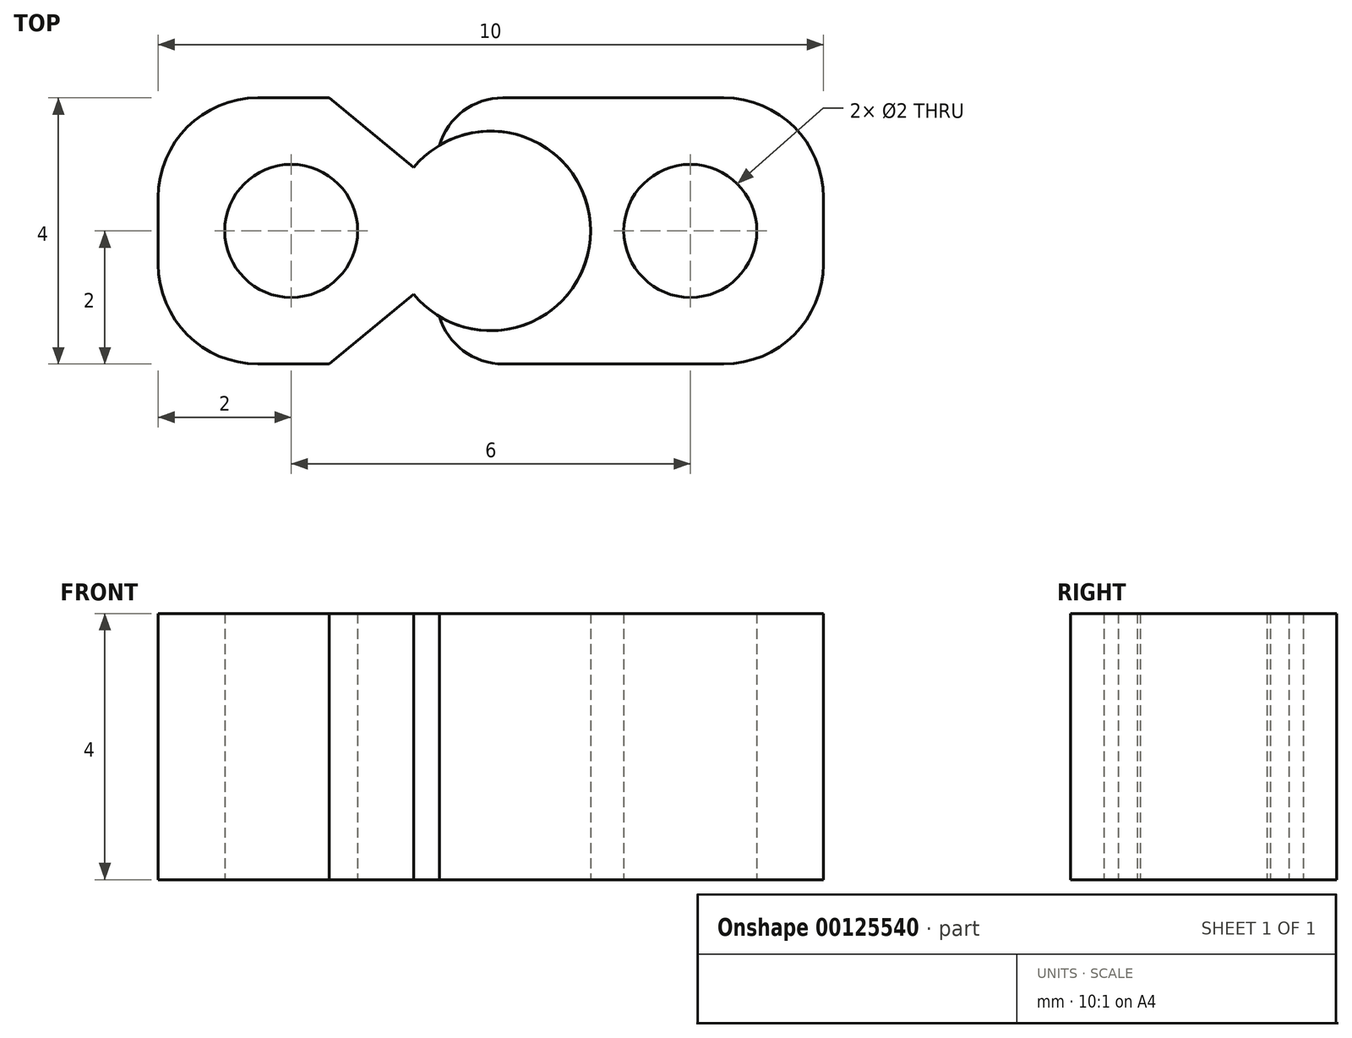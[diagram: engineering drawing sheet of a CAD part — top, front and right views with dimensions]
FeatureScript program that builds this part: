
annotation { "Feature Type Name" : "Feature", "Feature Type Description" : "" }
export const myFeature = defineFeature(function(context is Context, id is Id, definition is map)
    precondition{}
    {
        {
            var Q0;
            Q0=qCreatedBy(makeId("Top.planeOp"),FACE);
            var sketch = newSketch(context, id + "F0", { "sketchPlane" : qUnion([Q0])});
            skLineSegment(sketch, "E0.bottom", {"start": v(5, 2) * mm, "end": v(-5, 2) * mm});
            skLineSegment(sketch, "E0.top", {"start": v(5, -2) * mm, "end": v(-5, -2) * mm});
            skLineSegment(sketch, "E0.left", {"start": v(5, 2) * mm, "end": v(5, -2) * mm});
            skLineSegment(sketch, "E0.right", {"start": v(-5, 2) * mm, "end": v(-5, -2) * mm});
            skPoint(sketch, "E0.middle", {"position": v(0, 0) * mm});
            skCircle(sketch, "E1", {"center": v(0, 0) * mm, "radius": 1.5 * mm});
            skLineSegment(sketch, "E2", {"start": v(-1.16, 0.95) * mm, "end": v(-2.43, 2) * mm});
            skLineSegment(sketch, "E3.0", {"start": v(-0.77, 1.28) * mm, "end": v(-1.64, 2) * mm});
            skLineSegment(sketch, "E4.MirrorCS", {"start": v(-1.16, -0.95) * mm, "end": v(-2.43, -2) * mm});
            skLineSegment(sketch, "E5.MirrorCS", {"start": v(-0.77, -1.28) * mm, "end": v(-1.64, -2) * mm});
            skPoint(sketch, "E6", {"position": v(3, 0) * mm});
            skPoint(sketch, "E7.MirrorP", {"position": v(-3, 0) * mm});
            skSolve(sketch);
        }
        {
            var Q0;
            {var subQ3=sQuery(id+"F0.wireOp",EDGE,"E0.right");Q0=makeQuery(id+"F0.imprint","IMPRINT",FACE,{"disambiguationData":[TD([[makeQuery(id+"F0.imprint","IMPRINT",EDGE,{"derivedFrom":subQ3}),1.0]])]});}
            var Q1;
            {var subQ0=sQuery(id+"F0.wireOp",EDGE,"E1");var subQ1=makeQuery(id+"F0.imprint","INTERSECT",VERTEX,{"derivedFrom":[subQ0,sQuery(id+"F0.wireOp",EDGE,"E2")]});Q1=makeQuery(id+"F0.imprint","IMPRINT",FACE,{"disambiguationData":[TD([[makeQuery(id+"F0.imprint","IMPRINT",EDGE,{"disambiguationData":[TD([[subQ1,1.0]])],"derivedFrom":subQ0}),1.0]])]});}
            extrude(context, id + "F1", {"entities" : qUnion([Q0, Q1]), "depth" : 4 * mm});
        }
        {
            var Q0;
            {var subQ3=sQuery(id+"F0.wireOp",EDGE,"E0.left");Q0=makeQuery(id+"F0.imprint","IMPRINT",FACE,{"disambiguationData":[TD([[makeQuery(id+"F0.imprint","IMPRINT",EDGE,{"derivedFrom":subQ3}),-1.0]])]});}
            extrude(context, id + "F2", {"entities" : qUnion([Q0]), "depth" : 4 * mm});
        }
        {
            var Q0;
            Q0=makeQuery(id+"F1.opExtrude","SWEPT_EDGE",EDGE,{"disambiguationData":[OSD([sQuery(id+"F0.wireOp",EDGE,"E0.top"),sQuery(id+"F0.wireOp",EDGE,"E0.right")])]});
            var Q1;
            Q1=makeQuery(id+"F1.opExtrude","SWEPT_EDGE",EDGE,{"disambiguationData":[OSD([sQuery(id+"F0.wireOp",EDGE,"E0.bottom"),sQuery(id+"F0.wireOp",EDGE,"E0.right")])]});
            var Q2;
            Q2=makeQuery(id+"F2.opExtrude","SWEPT_EDGE",EDGE,{"disambiguationData":[OSD([sQuery(id+"F0.wireOp",EDGE,"E0.top"),sQuery(id+"F0.wireOp",EDGE,"E0.left")])]});
            var Q3;
            Q3=makeQuery(id+"F2.opExtrude","SWEPT_EDGE",EDGE,{"disambiguationData":[OSD([sQuery(id+"F0.wireOp",EDGE,"E0.bottom"),sQuery(id+"F0.wireOp",EDGE,"E0.left")])]});
            fillet(context, id + "F3", {"entities" : qUnion([Q0, Q1, Q2, Q3]), "radius" : 1.5 * mm, "tangentPropagation" : true, "allowEdgeOverflow" : false});
        }
        {
            var Q0;
            Q0=makeQuery(id+"F2.opExtrude","SWEPT_EDGE",EDGE,{"disambiguationData":[OSD([sQuery(id+"F0.wireOp",EDGE,"E0.bottom"),sQuery(id+"F0.wireOp",EDGE,"E3.0")])]});
            var Q1;
            Q1=makeQuery(id+"F2.opExtrude","SWEPT_EDGE",EDGE,{"disambiguationData":[OSD([sQuery(id+"F0.wireOp",EDGE,"E0.top"),sQuery(id+"F0.wireOp",EDGE,"E5.MirrorCS")])]});
            fillet(context, id + "F4", {"entities" : qUnion([Q0, Q1]), "radius" : 1 * mm, "tangentPropagation" : true, "allowEdgeOverflow" : false});
        }
        {
            var Q0;
            Q0=sQuery(id+"F0.wireOp",VERTEX,"E6");
            var Q1;
            Q1=sQuery(id+"F0.wireOp",VERTEX,"E7.MirrorP");
            var Q2;
            Q2=makeQuery(id+"F2.opExtrude","SWEPT_BODY",BODY,{"disambiguationData":[OSD([sQuery(id+"F0.wireOp",EDGE,"E0.bottom"),sQuery(id+"F0.wireOp",EDGE,"E0.top"),sQuery(id+"F0.wireOp",EDGE,"E0.left"),sQuery(id+"F0.wireOp",EDGE,"E1"),sQuery(id+"F0.wireOp",EDGE,"E3.0"),sQuery(id+"F0.wireOp",EDGE,"E5.MirrorCS")])]});
            var Q3;
            Q3=makeQuery(id+"F1.opExtrude","SWEPT_BODY",BODY,{"disambiguationData":[OSD([sQuery(id+"F0.wireOp",EDGE,"E0.bottom"),sQuery(id+"F0.wireOp",EDGE,"E0.top"),sQuery(id+"F0.wireOp",EDGE,"E0.right"),sQuery(id+"F0.wireOp",EDGE,"E1"),sQuery(id+"F0.wireOp",EDGE,"E2"),sQuery(id+"F0.wireOp",EDGE,"E4.MirrorCS")])]});
            hole(context, id + "F5", {"style" : HoleStyle.SIMPLE, "endStyle" : HoleEndStyle.THROUGH, "oppositeDirection" : true, "holeDiameter" : 2 * mm, "startFromSketch" : true, "locations" : qUnion([Q0, Q1]), "scope" : qUnion([Q2, Q3]), "isTappedThrough" : true});
        }
    });
